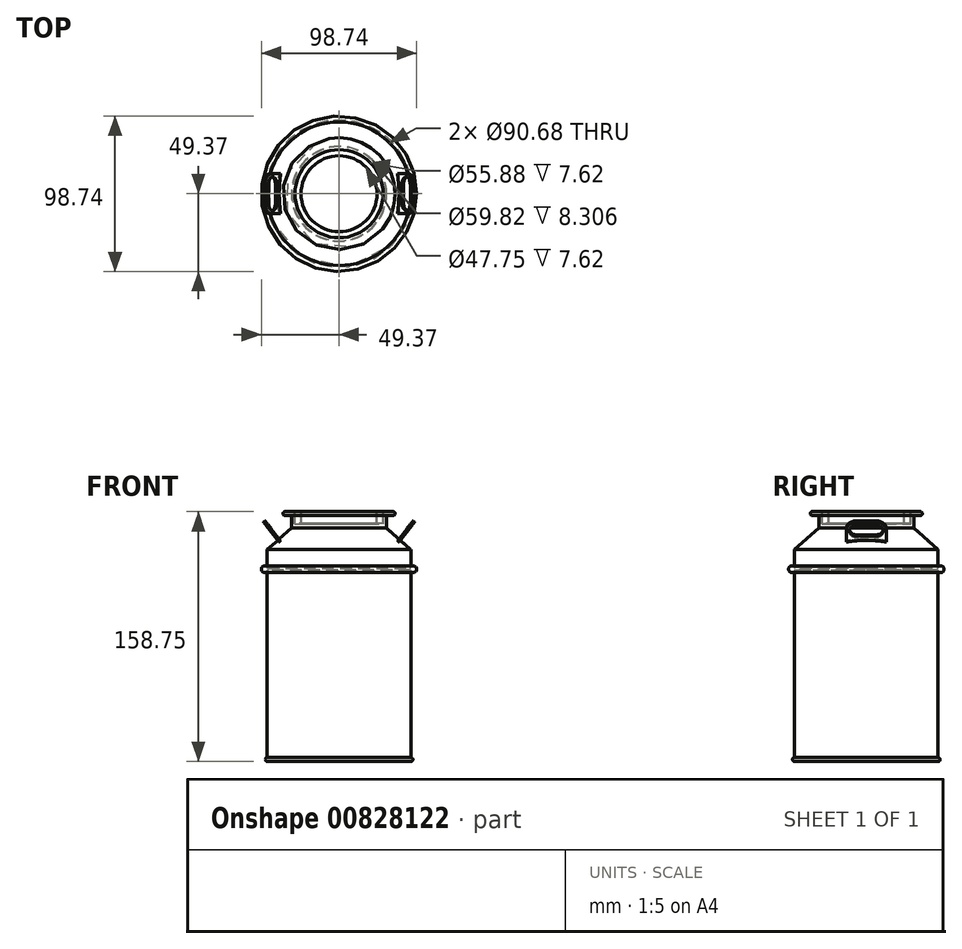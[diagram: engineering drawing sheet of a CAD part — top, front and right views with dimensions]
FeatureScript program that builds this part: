
annotation { "Feature Type Name" : "Feature", "Feature Type Description" : "" }
export const myFeature = defineFeature(function(context is Context, id is Id, definition is map)
    precondition{}
    {
        {
            var Q0;
            Q0=qCreatedBy(makeId("Front.planeOp"),FACE);
            var sketch = newSketch(context, id + "F0", { "sketchPlane" : qUnion([Q0])});
            skLineSegment(sketch, "E0", {"start": v(0, 0) * mm, "end": v(45.6, 0) * mm});
            skLineSegment(sketch, "E1", {"start": v(45.6, 2.54) * mm, "end": v(45.6, 120.65) * mm});
            skArc(sketch, "E2", {"start": v(45.6, 120.65) * mm, "mid": v(49.37, 122.15) * mm, "end": v(45.6, 123.64) * mm});
            skLineSegment(sketch, "E3", {"start": v(45.6, 123.64) * mm, "end": v(45.6, 134.54) * mm});
            skLineSegment(sketch, "E4", {"start": v(45.6, 134.54) * mm, "end": v(45.6, 134.54) * mm});
            skLineSegment(sketch, "E5", {"start": v(30.16, 148.23) * mm, "end": v(45.6, 134.54) * mm});
            skLineSegment(sketch, "E6", {"start": v(34.29, 158.75) * mm, "end": v(27.94, 158.75) * mm});
            skLineSegment(sketch, "E7", {"start": v(27.94, 158.75) * mm, "end": v(27.94, 151.13) * mm});
            skLineSegment(sketch, "E8", {"start": v(27.94, 151.13) * mm, "end": v(24.13, 151.13) * mm});
            skLineSegment(sketch, "E9", {"start": v(24.13, 151.13) * mm, "end": v(24.13, 158.75) * mm});
            skLineSegment(sketch, "E10", {"start": v(24.13, 158.75) * mm, "end": v(0, 158.75) * mm});
            skLineSegment(sketch, "E11", {"start": v(0, 158.75) * mm, "end": v(0, 0) * mm});
            skArc(sketch, "E12", {"start": v(34.29, 156.17) * mm, "mid": v(35.58, 157.46) * mm, "end": v(34.29, 158.75) * mm});
            skLineSegment(sketch, "E13", {"start": v(34.29, 156.17) * mm, "end": v(30.16, 156.17) * mm});
            skLineSegment(sketch, "E14", {"start": v(30.16, 156.17) * mm, "end": v(30.16, 148.23) * mm});
            skArc(sketch, "E15", {"start": v(45.6, 0) * mm, "mid": v(46.86, 1.27) * mm, "end": v(45.6, 2.54) * mm});
            skSolve(sketch);
        }
        {
            var Q0;
            Q0=makeQuery(id+"F0.imprint","IMPRINT",FACE,{"disambiguationData":[TD([[makeQuery(id+"F0.imprint","IMPRINT",EDGE,{"derivedFrom":sQuery(id+"F0.wireOp",EDGE,"E0")}),1.0]])]});
            var Q1;
            Q1=sQuery(id+"F0.wireOp",EDGE,"E11");
            revolve(context, id + "F1", {"surfaceOperationType" : NewSurfaceOperationType.NEW, "entities" : qUnion([Q0]), "axis" : qUnion([Q1]), "revolveType" : RevolveType.FULL});
        }
        {
            var Q0;
            Q0=qCreatedBy(makeId("Front.planeOp"),FACE);
            var sketch = newSketch(context, id + "F2", { "sketchPlane" : qUnion([Q0])});
            skLineSegment(sketch, "E16", {"start": v(35.23, 137.83) * mm, "end": v(46.96, 152.84) * mm});
            skLineSegment(sketch, "E17", {"start": v(46.96, 152.84) * mm, "end": v(47.96, 152.05) * mm});
            skLineSegment(sketch, "E18", {"start": v(47.96, 152.05) * mm, "end": v(36.23, 137.05) * mm});
            skLineSegment(sketch, "E19", {"start": v(36.23, 137.05) * mm, "end": v(35.23, 137.83) * mm});
            skLineSegment(sketch, "E20", {"start": v(0, 161.97) * mm, "end": v(0, 0) * mm, "construction": true});
            skLineSegment(sketch, "E21.MirrorCS", {"start": v(-35.23, 137.83) * mm, "end": v(-46.96, 152.84) * mm});
            skLineSegment(sketch, "E22.MirrorCS", {"start": v(-47.96, 152.05) * mm, "end": v(-36.23, 137.05) * mm});
            skLineSegment(sketch, "E23.MirrorCS", {"start": v(-46.96, 152.84) * mm, "end": v(-47.96, 152.05) * mm});
            skLineSegment(sketch, "E24.MirrorCS", {"start": v(-36.23, 137.05) * mm, "end": v(-35.23, 137.83) * mm});
            skSolve(sketch);
        }
        {
            var Q0;
            Q0 = qSketchRegion(id + "F2", true);
            extrude(context, id + "F3", {"entities" : qUnion([Q0]), "operationType" : NewBodyOperationType.ADD, "depth" : 12.7 * mm, "offsetDistance" : 25.4 * mm, "hasSecondDirection" : true, "secondDirectionOppositeDirection" : true, "secondDirectionDepth" : 12.7 * mm});
        }
        {
            var Q0;
            Q0=makeQuery(id+"F3.opExtrude","CAP_EDGE",EDGE,{"disambiguationData":[OSD([sQuery(id+"F2.wireOp",EDGE,"E17")])],"isStart":false});
            var Q1;
            Q1=makeQuery(id+"F3.opExtrude","CAP_EDGE",EDGE,{"disambiguationData":[OSD([sQuery(id+"F2.wireOp",EDGE,"E17")])],"isStart":true});
            fillet(context, id + "F4", {"entities" : qUnion([Q0, Q1]), "radius" : 6.35 * mm, "tangentPropagation" : true, "allowEdgeOverflow" : false});
        }
        {
            var Q0;
            Q0=makeQuery(id+"F3.opExtrude","CAP_EDGE",EDGE,{"disambiguationData":[OSD([sQuery(id+"F2.wireOp",EDGE,"E23.MirrorCS")])],"isStart":true});
            var Q1;
            Q1=makeQuery(id+"F3.opExtrude","CAP_EDGE",EDGE,{"disambiguationData":[OSD([sQuery(id+"F2.wireOp",EDGE,"E23.MirrorCS")])],"isStart":false});
            fillet(context, id + "F5", {"entities" : qUnion([Q0, Q1]), "radius" : 6.35 * mm, "tangentPropagation" : true, "allowEdgeOverflow" : false});
        }
        {
            var Q0;
            Q0=makeQuery(id+"F3.opExtrude","SWEPT_FACE",FACE,{"disambiguationData":[OSD([sQuery(id+"F2.wireOp",EDGE,"E18")])]});
            var sketch = newSketch(context, id + "F6", { "sketchPlane" : qUnion([Q0])});
            skArc(sketch, "E25", {"start": v(-6.3, 146.75) * mm, "mid": v(-10.62, 142.43) * mm, "end": v(-6.3, 138.11) * mm});
            skPoint(sketch, "E25.endSnap0", {"position": v(-12.7, 138.11) * mm});
            skArc(sketch, "E26", {"start": v(6.4, 138.11) * mm, "mid": v(10.72, 142.43) * mm, "end": v(6.4, 146.75) * mm});
            skLineSegment(sketch, "E27", {"start": v(-6.3, 146.75) * mm, "end": v(6.4, 146.75) * mm});
            skLineSegment(sketch, "E28", {"start": v(-6.3, 138.11) * mm, "end": v(6.4, 138.11) * mm});
            skSolve(sketch);
        }
        {
            var Q0;
            Q0=makeQuery(id+"F6.imprint","IMPRINT",FACE,{"disambiguationData":[TD([[makeQuery(id+"F6.imprint","IMPRINT",EDGE,{"derivedFrom":sQuery(id+"F6.wireOp",EDGE,"E25")}),1.0]])]});
            extrude(context, id + "F7", {"entities" : qUnion([Q0]), "operationType" : NewBodyOperationType.REMOVE, "oppositeDirection" : true, "depth" : 5.08 * mm, "offsetDistance" : 25.4 * mm});
        }
        {
            var Q0;
            Q0=makeQuery(id+"F3.opExtrude","SWEPT_FACE",FACE,{"disambiguationData":[OSD([sQuery(id+"F2.wireOp",EDGE,"E22.MirrorCS")])]});
            var sketch = newSketch(context, id + "F8", { "sketchPlane" : qUnion([Q0])});
            skArc(sketch, "E29", {"start": v(-6.35, 145.76) * mm, "mid": v(-10.67, 141.45) * mm, "end": v(-6.35, 137.13) * mm});
            skArc(sketch, "E30", {"start": v(6.35, 137.13) * mm, "mid": v(10.67, 141.45) * mm, "end": v(6.35, 145.76) * mm});
            skLineSegment(sketch, "E31", {"start": v(-6.35, 145.76) * mm, "end": v(6.35, 145.76) * mm});
            skLineSegment(sketch, "E32", {"start": v(-6.35, 137.13) * mm, "end": v(6.35, 137.13) * mm});
            skSolve(sketch);
        }
        {
            var Q0;
            Q0=makeQuery(id+"F8.imprint","IMPRINT",FACE,{"disambiguationData":[TD([[makeQuery(id+"F8.imprint","IMPRINT",EDGE,{"derivedFrom":sQuery(id+"F8.wireOp",EDGE,"E29")}),1.0]])]});
            var Q1;
            Q1=sQuery(id+"F8.wireOp",EDGE,"E29");
            var Q2;
            Q2=sQuery(id+"F8.wireOp",EDGE,"E30");
            var Q3;
            Q3=sQuery(id+"F8.wireOp",EDGE,"E31");
            var Q4;
            Q4=sQuery(id+"F8.wireOp",EDGE,"E32");
            extrude(context, id + "F9", {"entities" : qUnion([Q0]), "operationType" : NewBodyOperationType.REMOVE, "surfaceEntities" : qUnion([Q1, Q2, Q3, Q4]), "oppositeDirection" : true, "depth" : 5.08 * mm, "offsetDistance" : 25.4 * mm});
        }
        {
            var Q0;
            Q0=makeQuery(id+"F1.opRevolve","SWEPT_FACE",FACE,{"disambiguationData":[OSD([sQuery(id+"F0.wireOp",EDGE,"E5")])]});
            var Q1;
            Q1=makeQuery(id+"F1.opRevolve","SWEPT_BODY",BODY,{"disambiguationData":[OSD([sQuery(id+"F0.wireOp",EDGE,"E0"),sQuery(id+"F0.wireOp",EDGE,"E1"),sQuery(id+"F0.wireOp",EDGE,"E2"),sQuery(id+"F0.wireOp",EDGE,"E3"),sQuery(id+"F0.wireOp",EDGE,"E5"),sQuery(id+"F0.wireOp",EDGE,"E6"),sQuery(id+"F0.wireOp",EDGE,"E7"),sQuery(id+"F0.wireOp",EDGE,"E8"),sQuery(id+"F0.wireOp",EDGE,"E9"),sQuery(id+"F0.wireOp",EDGE,"E10"),sQuery(id+"F0.wireOp",EDGE,"E11"),sQuery(id+"F0.wireOp",EDGE,"E12"),sQuery(id+"F0.wireOp",EDGE,"E13"),sQuery(id+"F0.wireOp",EDGE,"E14"),sQuery(id+"F0.wireOp",EDGE,"E15")])]});
            shell(context, id + "F10", {"isHollow" : true, "entities" : qUnion([Q0]), "parts" : qUnion([Q1]), "thickness" : 0.25 * mm});
        }
    });
